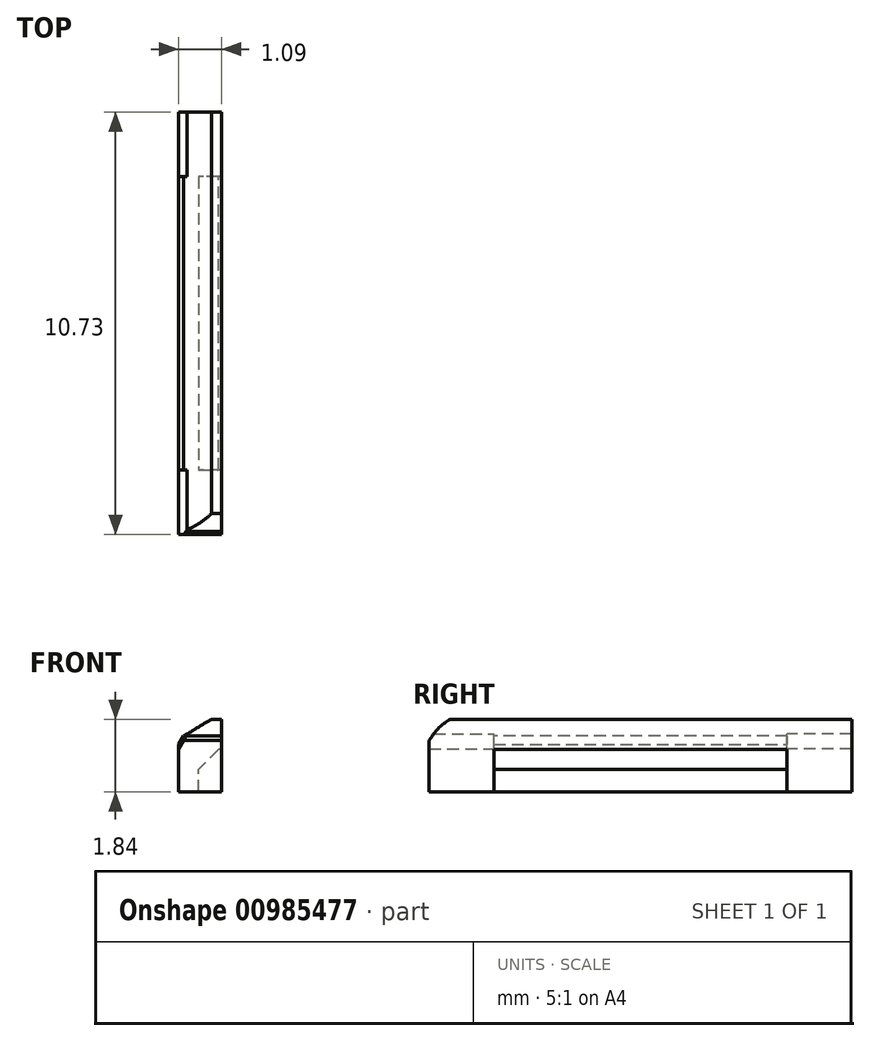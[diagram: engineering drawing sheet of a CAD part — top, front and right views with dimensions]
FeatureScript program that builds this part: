
annotation { "Feature Type Name" : "Feature", "Feature Type Description" : "" }
export const myFeature = defineFeature(function(context is Context, id is Id, definition is map)
    precondition{}
    {
        {
            var Q0;
            Q0=qCreatedBy(makeId("Front.planeOp"),FACE);
            var sketch = newSketch(context, id + "F0", { "sketchPlane" : qUnion([Q0])});
            skLineSegment(sketch, "E0.bottom", {"start": v(0, 0) * mm, "end": v(1.1, 0) * mm});
            skLineSegment(sketch, "E0.left", {"start": v(0, 0) * mm, "end": v(0, 1.34) * mm});
            skLineSegment(sketch, "E0.right", {"start": v(1.1, 0) * mm, "end": v(1.1, 1.09) * mm});
            skLineSegment(sketch, "E1", {"start": v(0, 1.34) * mm, "end": v(1.1, 2) * mm});
            skLineSegment(sketch, "E2", {"start": v(1.1, 2) * mm, "end": v(1.1, 1.09) * mm});
            skSolve(sketch);
        }
        {
            var Q0;
            Q0=qSketchRegion(id+"F0",true);
            extrude(context, id + "F1", {"entities" : qUnion([Q0]), "depth" : 7.45 * mm});
        }
        {
            var Q0;
            Q0=makeQuery(id+"F1.opExtrude","CAP_FACE",FACE,{"disambiguationData":[OSD([sQuery(id+"F0.wireOp",EDGE,"E0.bottom"),sQuery(id+"F0.wireOp",EDGE,"E0.left"),sQuery(id+"F0.wireOp",EDGE,"E0.right"),sQuery(id+"F0.wireOp",EDGE,"E1"),sQuery(id+"F0.wireOp",EDGE,"E2")])],"isStart":false});
            var sketch = newSketch(context, id + "F2", { "sketchPlane" : qUnion([Q0])});
            skLineSegment(sketch, "E3.bottom", {"start": v(1.1, 0) * mm, "end": v(0.51, 0) * mm});
            skLineSegment(sketch, "E3.top", {"start": v(1.1, 1.07) * mm, "end": v(0.51, 1.07) * mm});
            skLineSegment(sketch, "E3.left", {"start": v(1.1, 0) * mm, "end": v(1.1, 1.07) * mm});
            skLineSegment(sketch, "E3.right", {"start": v(0.51, 0) * mm, "end": v(0.51, 1.07) * mm});
            skSolve(sketch);
        }
        {
            var Q0;
            Q0=qSketchRegion(id+"F2",true);
            extrude(context, id + "F3", {"entities" : qUnion([Q0]), "operationType" : NewBodyOperationType.REMOVE, "endBound" : BoundingType.THROUGH_ALL, "oppositeDirection" : true, "depth" : 25 * mm});
        }
        {
            var Q0;
            Q0=makeQuery(id+"F3.boolean.opBoolean","COPY",EDGE,{"derivedFrom":makeQuery(id+"F3.opExtrude","SWEPT_EDGE",EDGE,{"disambiguationData":[OSD([sQuery(id+"F2.wireOp",EDGE,"E3.top"),sQuery(id+"F2.wireOp",EDGE,"E3.right")])]})});
            chamfer(context, id + "F4", {"entities" : qUnion([Q0]), "width" : .5 * mm, "tangentPropagation" : true});
        }
        {
            var Q0;
            Q0=makeQuery(id+"F1.opExtrude","SWEPT_EDGE",EDGE,{"disambiguationData":[OSD([sQuery(id+"F0.wireOp",EDGE,"E0.left"),sQuery(id+"F0.wireOp",EDGE,"E1")])]});
            chamfer(context, id + "F5", {"entities" : qUnion([Q0]), "width" : .25 * mm, "tangentPropagation" : true});
        }
        {
            var Q0;
            Q0=makeQuery(id+"F1.opExtrude","CAP_FACE",FACE,{"disambiguationData":[OSD([sQuery(id+"F0.wireOp",EDGE,"E0.bottom"),sQuery(id+"F0.wireOp",EDGE,"E0.left"),sQuery(id+"F0.wireOp",EDGE,"E0.right"),sQuery(id+"F0.wireOp",EDGE,"E1"),sQuery(id+"F0.wireOp",EDGE,"E2")])],"isStart":true});
            var sketch = newSketch(context, id + "F6", { "sketchPlane" : qUnion([Q0])});
            skLineSegment(sketch, "E4", {"start": v(-1.1, 2) * mm, "end": v(-1.1, 0) * mm});
            skLineSegment(sketch, "E5", {"start": v(-1.1, 0) * mm, "end": v(0, 0) * mm});
            skLineSegment(sketch, "E6", {"start": v(0, 0) * mm, "end": v(0, 1.1) * mm});
            skLineSegment(sketch, "E7", {"start": v(0, 1.1) * mm, "end": v(-0.21, 1.47) * mm});
            skLineSegment(sketch, "E8", {"start": v(-0.21, 1.47) * mm, "end": v(-1.1, 2) * mm});
            skSolve(sketch);
        }
        {
            var Q0;
            Q0=qSketchRegion(id+"F6",true);
            extrude(context, id + "F7", {"entities" : qUnion([Q0]), "operationType" : NewBodyOperationType.ADD, "depth" : ((2 - 1.45 / 2) + 0.37) * mm});
        }
        {
            var Q0;
            Q0=makeQuery(id+"F1.opExtrude","CAP_FACE",FACE,{"disambiguationData":[OSD([sQuery(id+"F0.wireOp",EDGE,"E0.bottom"),sQuery(id+"F0.wireOp",EDGE,"E0.left"),sQuery(id+"F0.wireOp",EDGE,"E0.right"),sQuery(id+"F0.wireOp",EDGE,"E1"),sQuery(id+"F0.wireOp",EDGE,"E2")])],"isStart":false});
            var sketch = newSketch(context, id + "F8", { "sketchPlane" : qUnion([Q0])});
            skLineSegment(sketch, "E9", {"start": v(1.1, 2) * mm, "end": v(1.1, 0) * mm});
            skLineSegment(sketch, "E10", {"start": v(1.1, 0) * mm, "end": v(0, 0) * mm});
            skLineSegment(sketch, "E11", {"start": v(0, 0) * mm, "end": v(0, 1.1) * mm});
            skLineSegment(sketch, "E12", {"start": v(0, 1.1) * mm, "end": v(0.21, 1.47) * mm});
            skLineSegment(sketch, "E13", {"start": v(0.21, 1.47) * mm, "end": v(1.1, 2) * mm});
            skSolve(sketch);
        }
        {
            var Q0;
            Q0=qSketchRegion(id+"F8",true);
            extrude(context, id + "F9", {"entities" : qUnion([Q0]), "operationType" : NewBodyOperationType.ADD, "depth" : ((2 - 1.45 / 2) + 0.37) * mm});
        }
        {
            var Q0;
            Q0=makeQuery(id+"F9.boolean.opBoolean","MERGE",FACE,{"derivedFrom":[makeQuery(id+"F7.boolean.opBoolean","MERGE",FACE,{"derivedFrom":[makeQuery(id+"F1.opExtrude","SWEPT_FACE",FACE,{"disambiguationData":[OSD([sQuery(id+"F0.wireOp",EDGE,"E0.right"),sQuery(id+"F0.wireOp",EDGE,"E2")])]}),makeQuery(id+"F7.opExtrude","SWEPT_FACE",FACE,{"disambiguationData":[OSD([sQuery(id+"F6.wireOp",EDGE,"E4")])]})]}),makeQuery(id+"F9.opExtrude","SWEPT_FACE",FACE,{"disambiguationData":[OSD([sQuery(id+"F8.wireOp",EDGE,"E9")])]})]});
            var sketch = newSketch(context, id + "F10", { "sketchPlane" : qUnion([Q0])});
            skLineSegment(sketch, "E14", {"start": v(-9.1, 1.31) * mm, "end": v(-9, 1.42) * mm});
            skArc(sketch, "E15", {"start": v(-7.62, 2) * mm, "mid": v(-8.4, 1.92) * mm, "end": v(-9, 1.42) * mm});
            skLineSegment(sketch, "E16", {"start": v(-9.1, 1.31) * mm, "end": v(-9.1, 2) * mm});
            skLineSegment(sketch, "E17", {"start": v(-9.1, 2) * mm, "end": v(-7.62, 2) * mm});
            skSolve(sketch);
        }
        {
            var Q0;
            Q0=makeQuery(id+"F9.boolean.opBoolean","MERGE",FACE,{"derivedFrom":[makeQuery(id+"F7.boolean.opBoolean","MERGE",FACE,{"derivedFrom":[makeQuery(id+"F1.opExtrude","SWEPT_FACE",FACE,{"disambiguationData":[OSD([sQuery(id+"F0.wireOp",EDGE,"E0.right"),sQuery(id+"F0.wireOp",EDGE,"E2")])]}),makeQuery(id+"F7.opExtrude","SWEPT_FACE",FACE,{"disambiguationData":[OSD([sQuery(id+"F6.wireOp",EDGE,"E4")])]})]}),makeQuery(id+"F9.opExtrude","SWEPT_FACE",FACE,{"disambiguationData":[OSD([sQuery(id+"F8.wireOp",EDGE,"E9")])]})]});
            var sketch = newSketch(context, id + "F11", { "sketchPlane" : qUnion([Q0])});
            skLineSegment(sketch, "E18.bottom", {"start": v(1.64, 2) * mm, "end": v(-9.1, 2) * mm});
            skLineSegment(sketch, "E18.top", {"start": v(1.64, 1.84) * mm, "end": v(-9.1, 1.84) * mm});
            skLineSegment(sketch, "E18.left", {"start": v(1.64, 2) * mm, "end": v(1.64, 1.84) * mm});
            skLineSegment(sketch, "E18.right", {"start": v(-9.1, 2) * mm, "end": v(-9.1, 1.84) * mm});
            skSolve(sketch);
        }
        {
            var Q0;
            Q0=qSketchRegion(id+"F11",true);
            extrude(context, id + "F12", {"entities" : qUnion([Q0]), "operationType" : NewBodyOperationType.REMOVE, "endBound" : BoundingType.THROUGH_ALL, "oppositeDirection" : true, "depth" : 25 * mm});
        }
        {
            var Q0;
            Q0=qSketchRegion(id+"F10",true);
            extrude(context, id + "F13", {"entities" : qUnion([Q0]), "operationType" : NewBodyOperationType.REMOVE, "endBound" : BoundingType.THROUGH_ALL, "oppositeDirection" : true, "depth" : 25 * mm});
        }
    });
